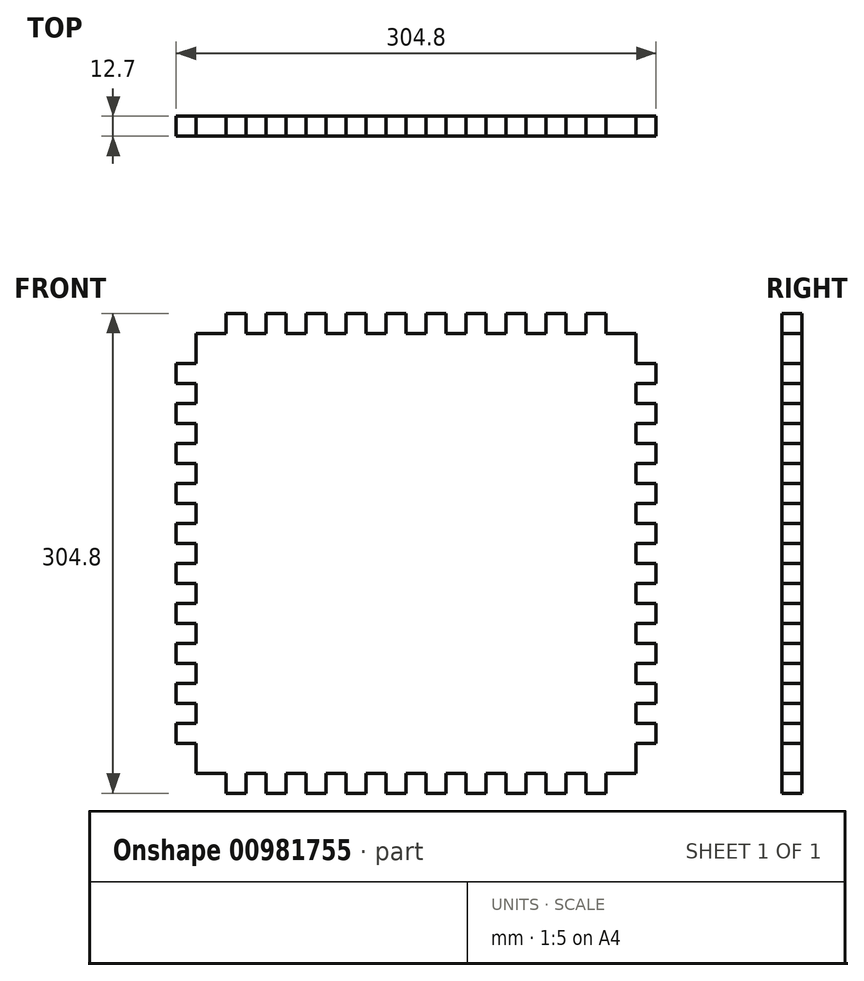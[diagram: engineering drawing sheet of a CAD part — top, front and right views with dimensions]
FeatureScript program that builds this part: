
annotation { "Feature Type Name" : "Feature", "Feature Type Description" : "" }
export const myFeature = defineFeature(function(context is Context, id is Id, definition is map)
    precondition{}
    {
        {
            var Q0;
            Q0=qCreatedBy(makeId("Front.planeOp"),FACE);
            var sketch = newSketch(context, id + "F0", { "sketchPlane" : qUnion([Q0])});
            skPoint(sketch, "E0.middle", {"position": v(0, 0) * mm});
            skLineSegment(sketch, "E1", {"start": v(-120.65, 139.7) * mm, "end": v(-120.65, 152.4) * mm});
            skLineSegment(sketch, "E2", {"start": v(-120.65, 152.4) * mm, "end": v(-107.95, 152.4) * mm});
            skLineSegment(sketch, "E3", {"start": v(-107.95, 152.4) * mm, "end": v(-107.95, 139.7) * mm});
            skLineSegment(sketch, "E4", {"start": v(-107.95, 139.7) * mm, "end": v(-95.25, 139.7) * mm});
            skLineSegment(sketch, "E5", {"start": v(-120.65, 139.7) * mm, "end": v(-139.7, 139.7) * mm});
            skLineSegment(sketch, "E6.1.0.0", {"start": v(-95.25, 152.4) * mm, "end": v(-82.55, 152.4) * mm});
            skLineSegment(sketch, "E6.1.0.1", {"start": v(-95.25, 139.7) * mm, "end": v(-95.25, 152.4) * mm});
            skLineSegment(sketch, "E6.1.0.2", {"start": v(-82.55, 139.7) * mm, "end": v(-69.85, 139.7) * mm});
            skLineSegment(sketch, "E6.1.0.3", {"start": v(-82.55, 152.4) * mm, "end": v(-82.55, 139.7) * mm});
            skLineSegment(sketch, "E6.2.0.0", {"start": v(-69.85, 152.4) * mm, "end": v(-57.15, 152.4) * mm});
            skLineSegment(sketch, "E6.2.0.1", {"start": v(-69.85, 139.7) * mm, "end": v(-69.85, 152.4) * mm});
            skLineSegment(sketch, "E6.2.0.2", {"start": v(-57.15, 139.7) * mm, "end": v(-44.45, 139.7) * mm});
            skLineSegment(sketch, "E6.2.0.3", {"start": v(-57.15, 152.4) * mm, "end": v(-57.15, 139.7) * mm});
            skLineSegment(sketch, "E6.3.0.0", {"start": v(-44.45, 152.4) * mm, "end": v(-31.75, 152.4) * mm});
            skLineSegment(sketch, "E6.3.0.1", {"start": v(-44.45, 139.7) * mm, "end": v(-44.45, 152.4) * mm});
            skLineSegment(sketch, "E6.3.0.2", {"start": v(-31.75, 139.7) * mm, "end": v(-19.05, 139.7) * mm});
            skLineSegment(sketch, "E6.3.0.3", {"start": v(-31.75, 152.4) * mm, "end": v(-31.75, 139.7) * mm});
            skLineSegment(sketch, "E6.4.0.0", {"start": v(-19.05, 152.4) * mm, "end": v(-6.35, 152.4) * mm});
            skLineSegment(sketch, "E6.4.0.1", {"start": v(-19.05, 139.7) * mm, "end": v(-19.05, 152.4) * mm});
            skLineSegment(sketch, "E6.4.0.2", {"start": v(-6.35, 139.7) * mm, "end": v(6.35, 139.7) * mm});
            skLineSegment(sketch, "E6.4.0.3", {"start": v(-6.35, 152.4) * mm, "end": v(-6.35, 139.7) * mm});
            skLineSegment(sketch, "E6.5.0.0", {"start": v(6.35, 152.4) * mm, "end": v(19.05, 152.4) * mm});
            skLineSegment(sketch, "E6.5.0.1", {"start": v(6.35, 139.7) * mm, "end": v(6.35, 152.4) * mm});
            skLineSegment(sketch, "E6.5.0.2", {"start": v(19.05, 139.7) * mm, "end": v(31.75, 139.7) * mm});
            skLineSegment(sketch, "E6.5.0.3", {"start": v(19.05, 152.4) * mm, "end": v(19.05, 139.7) * mm});
            skLineSegment(sketch, "E6.6.0.0", {"start": v(31.75, 152.4) * mm, "end": v(44.45, 152.4) * mm});
            skLineSegment(sketch, "E6.6.0.1", {"start": v(31.75, 139.7) * mm, "end": v(31.75, 152.4) * mm});
            skLineSegment(sketch, "E6.6.0.2", {"start": v(44.45, 139.7) * mm, "end": v(57.15, 139.7) * mm});
            skLineSegment(sketch, "E6.6.0.3", {"start": v(44.45, 152.4) * mm, "end": v(44.45, 139.7) * mm});
            skLineSegment(sketch, "E6.7.0.0", {"start": v(57.15, 152.4) * mm, "end": v(69.85, 152.4) * mm});
            skLineSegment(sketch, "E6.7.0.1", {"start": v(57.15, 139.7) * mm, "end": v(57.15, 152.4) * mm});
            skLineSegment(sketch, "E6.7.0.2", {"start": v(69.85, 139.7) * mm, "end": v(82.55, 139.7) * mm});
            skLineSegment(sketch, "E6.7.0.3", {"start": v(69.85, 152.4) * mm, "end": v(69.85, 139.7) * mm});
            skLineSegment(sketch, "E6.8.0.0", {"start": v(82.55, 152.4) * mm, "end": v(95.25, 152.4) * mm});
            skLineSegment(sketch, "E6.8.0.1", {"start": v(82.55, 139.7) * mm, "end": v(82.55, 152.4) * mm});
            skLineSegment(sketch, "E6.8.0.2", {"start": v(95.25, 139.7) * mm, "end": v(107.95, 139.7) * mm});
            skLineSegment(sketch, "E6.8.0.3", {"start": v(95.25, 152.4) * mm, "end": v(95.25, 139.7) * mm});
            skLineSegment(sketch, "E6.9.0.0", {"start": v(107.95, 152.4) * mm, "end": v(120.65, 152.4) * mm});
            skLineSegment(sketch, "E6.9.0.1", {"start": v(107.95, 139.7) * mm, "end": v(107.95, 152.4) * mm});
            skLineSegment(sketch, "E6.9.0.3", {"start": v(120.65, 152.4) * mm, "end": v(120.65, 139.7) * mm});
            skLineSegment(sketch, "E6.direction1", {"start": v(-120.65, 139.7) * mm, "end": v(-95.25, 139.7) * mm, "construction": true});
            skLineSegment(sketch, "E7", {"start": v(120.65, 139.7) * mm, "end": v(139.7, 139.7) * mm});
            skLineSegment(sketch, "E8.MirrorCS", {"start": v(-120.65, -139.7) * mm, "end": v(-95.25, -139.7) * mm, "construction": true});
            skLineSegment(sketch, "E9.MirrorCS", {"start": v(-95.25, -139.7) * mm, "end": v(-95.25, -152.4) * mm});
            skLineSegment(sketch, "E10.MirrorCS", {"start": v(-107.95, -152.4) * mm, "end": v(-107.95, -139.7) * mm});
            skLineSegment(sketch, "E11.MirrorCS", {"start": v(-107.95, -139.7) * mm, "end": v(-95.25, -139.7) * mm});
            skLineSegment(sketch, "E12.MirrorCS", {"start": v(-120.65, -152.4) * mm, "end": v(-107.95, -152.4) * mm});
            skLineSegment(sketch, "E13.MirrorCS", {"start": v(-95.25, -152.4) * mm, "end": v(-82.55, -152.4) * mm});
            skLineSegment(sketch, "E14.MirrorCS", {"start": v(-120.65, -139.7) * mm, "end": v(-120.65, -152.4) * mm});
            skLineSegment(sketch, "E15.MirrorCS", {"start": v(82.55, -139.7) * mm, "end": v(82.55, -152.4) * mm});
            skLineSegment(sketch, "E16.MirrorCS", {"start": v(82.55, -152.4) * mm, "end": v(95.25, -152.4) * mm});
            skLineSegment(sketch, "E17.MirrorCS", {"start": v(6.35, -152.4) * mm, "end": v(19.05, -152.4) * mm});
            skLineSegment(sketch, "E18.MirrorCS", {"start": v(-44.45, -152.4) * mm, "end": v(-31.75, -152.4) * mm});
            skLineSegment(sketch, "E19.MirrorCS", {"start": v(-31.75, -139.7) * mm, "end": v(-19.05, -139.7) * mm});
            skLineSegment(sketch, "E20.MirrorCS", {"start": v(-19.05, -152.4) * mm, "end": v(-6.35, -152.4) * mm});
            skLineSegment(sketch, "E21.MirrorCS", {"start": v(-82.55, -139.7) * mm, "end": v(-69.85, -139.7) * mm});
            skLineSegment(sketch, "E22.MirrorCS", {"start": v(-31.75, -152.4) * mm, "end": v(-31.75, -139.7) * mm});
            skLineSegment(sketch, "E23.MirrorCS", {"start": v(44.45, -152.4) * mm, "end": v(44.45, -139.7) * mm});
            skLineSegment(sketch, "E24.MirrorCS", {"start": v(31.75, -139.7) * mm, "end": v(31.75, -152.4) * mm});
            skLineSegment(sketch, "E25.MirrorCS", {"start": v(107.95, -139.7) * mm, "end": v(107.95, -152.4) * mm});
            skLineSegment(sketch, "E26.MirrorCS", {"start": v(-19.05, -139.7) * mm, "end": v(-19.05, -152.4) * mm});
            skLineSegment(sketch, "E27.MirrorCS", {"start": v(-69.85, -139.7) * mm, "end": v(-69.85, -152.4) * mm});
            skLineSegment(sketch, "E28.MirrorCS", {"start": v(107.95, -152.4) * mm, "end": v(120.65, -152.4) * mm});
            skLineSegment(sketch, "E29.MirrorCS", {"start": v(95.25, -152.4) * mm, "end": v(95.25, -139.7) * mm});
            skLineSegment(sketch, "E30.MirrorCS", {"start": v(31.75, -152.4) * mm, "end": v(44.45, -152.4) * mm});
            skLineSegment(sketch, "E31.MirrorCS", {"start": v(-6.35, -139.7) * mm, "end": v(6.35, -139.7) * mm});
            skLineSegment(sketch, "E32.MirrorCS", {"start": v(-69.85, -152.4) * mm, "end": v(-57.15, -152.4) * mm});
            skLineSegment(sketch, "E33.MirrorCS", {"start": v(69.85, -139.7) * mm, "end": v(82.55, -139.7) * mm});
            skLineSegment(sketch, "E34.MirrorCS", {"start": v(-6.35, -152.4) * mm, "end": v(-6.35, -139.7) * mm});
            skLineSegment(sketch, "E35.MirrorCS", {"start": v(57.15, -152.4) * mm, "end": v(69.85, -152.4) * mm});
            skLineSegment(sketch, "E36.MirrorCS", {"start": v(-44.45, -139.7) * mm, "end": v(-44.45, -152.4) * mm});
            skLineSegment(sketch, "E37.MirrorCS", {"start": v(-57.15, -139.7) * mm, "end": v(-44.45, -139.7) * mm});
            skLineSegment(sketch, "E38.MirrorCS", {"start": v(-120.65, -139.7) * mm, "end": v(-139.7, -139.7) * mm});
            skLineSegment(sketch, "E39.MirrorCS", {"start": v(-82.55, -152.4) * mm, "end": v(-82.55, -139.7) * mm});
            skLineSegment(sketch, "E40.MirrorCS", {"start": v(44.45, -139.7) * mm, "end": v(57.15, -139.7) * mm});
            skLineSegment(sketch, "E41.MirrorCS", {"start": v(95.25, -139.7) * mm, "end": v(107.95, -139.7) * mm});
            skLineSegment(sketch, "E42.MirrorCS", {"start": v(57.15, -139.7) * mm, "end": v(57.15, -152.4) * mm});
            skLineSegment(sketch, "E43.MirrorCS", {"start": v(69.85, -152.4) * mm, "end": v(69.85, -139.7) * mm});
            skLineSegment(sketch, "E44.MirrorCS", {"start": v(120.65, -152.4) * mm, "end": v(120.65, -139.7) * mm});
            skLineSegment(sketch, "E45.MirrorCS", {"start": v(-57.15, -152.4) * mm, "end": v(-57.15, -139.7) * mm});
            skLineSegment(sketch, "E46.MirrorCS", {"start": v(19.05, -152.4) * mm, "end": v(19.05, -139.7) * mm});
            skLineSegment(sketch, "E47.MirrorCS", {"start": v(120.65, -139.7) * mm, "end": v(139.7, -139.7) * mm});
            skLineSegment(sketch, "E48.MirrorCS", {"start": v(19.05, -139.7) * mm, "end": v(31.75, -139.7) * mm});
            skLineSegment(sketch, "E49.MirrorCS", {"start": v(6.35, -139.7) * mm, "end": v(6.35, -152.4) * mm});
            skLineSegment(sketch, "E50.MirrorCS", {"start": v(-152.4, 107.95) * mm, "end": v(-139.7, 107.95) * mm});
            skLineSegment(sketch, "E51.MirrorCS", {"start": v(-139.7, 107.95) * mm, "end": v(-139.7, 95.25) * mm});
            skLineSegment(sketch, "E52.MirrorCS", {"start": v(-152.4, 120.65) * mm, "end": v(-152.4, 107.95) * mm});
            skLineSegment(sketch, "E53.MirrorCS", {"start": v(-152.4, -107.95) * mm, "end": v(-152.4, -120.65) * mm});
            skLineSegment(sketch, "E54.MirrorCS", {"start": v(-139.7, 44.45) * mm, "end": v(-152.4, 44.45) * mm});
            skLineSegment(sketch, "E55.MirrorCS", {"start": v(-139.7, 69.85) * mm, "end": v(-152.4, 69.85) * mm});
            skLineSegment(sketch, "E56.MirrorCS", {"start": v(-152.4, -95.25) * mm, "end": v(-139.7, -95.25) * mm});
            skLineSegment(sketch, "E57.MirrorCS", {"start": v(-139.7, 6.35) * mm, "end": v(-139.7, -6.35) * mm});
            skLineSegment(sketch, "E58.MirrorCS", {"start": v(-139.7, 82.55) * mm, "end": v(-139.7, 69.85) * mm});
            skLineSegment(sketch, "E59.MirrorCS", {"start": v(-152.4, -31.75) * mm, "end": v(-152.4, -44.45) * mm});
            skLineSegment(sketch, "E60.MirrorCS", {"start": v(-139.7, -6.35) * mm, "end": v(-152.4, -6.35) * mm});
            skLineSegment(sketch, "E61.MirrorCS", {"start": v(-139.7, -95.25) * mm, "end": v(-139.7, -107.95) * mm});
            skLineSegment(sketch, "E62.MirrorCS", {"start": v(-139.7, -69.85) * mm, "end": v(-139.7, -82.55) * mm});
            skLineSegment(sketch, "E63.MirrorCS", {"start": v(-139.7, 95.25) * mm, "end": v(-152.4, 95.25) * mm});
            skLineSegment(sketch, "E64.MirrorCS", {"start": v(-139.7, 19.05) * mm, "end": v(-152.4, 19.05) * mm});
            skLineSegment(sketch, "E65.MirrorCS", {"start": v(-139.7, -31.75) * mm, "end": v(-152.4, -31.75) * mm});
            skLineSegment(sketch, "E66.MirrorCS", {"start": v(-152.4, 95.25) * mm, "end": v(-152.4, 82.55) * mm});
            skLineSegment(sketch, "E67.MirrorCS", {"start": v(-152.4, 69.85) * mm, "end": v(-152.4, 57.15) * mm});
            skLineSegment(sketch, "E68.MirrorCS", {"start": v(-152.4, 6.35) * mm, "end": v(-139.7, 6.35) * mm});
            skLineSegment(sketch, "E69.MirrorCS", {"start": v(-152.4, 31.75) * mm, "end": v(-139.7, 31.75) * mm});
            skLineSegment(sketch, "E70.MirrorCS", {"start": v(-152.4, -69.85) * mm, "end": v(-139.7, -69.85) * mm});
            skLineSegment(sketch, "E71.MirrorCS", {"start": v(-139.7, -82.55) * mm, "end": v(-152.4, -82.55) * mm});
            skLineSegment(sketch, "E72.MirrorCS", {"start": v(-152.4, 19.05) * mm, "end": v(-152.4, 6.35) * mm});
            skLineSegment(sketch, "E73.MirrorCS", {"start": v(-152.4, 82.55) * mm, "end": v(-139.7, 82.55) * mm});
            skLineSegment(sketch, "E74.MirrorCS", {"start": v(-152.4, -6.35) * mm, "end": v(-152.4, -19.05) * mm});
            skLineSegment(sketch, "E75.MirrorCS", {"start": v(-152.4, -82.55) * mm, "end": v(-152.4, -95.25) * mm});
            skLineSegment(sketch, "E76.MirrorCS", {"start": v(-152.4, -57.15) * mm, "end": v(-152.4, -69.85) * mm});
            skLineSegment(sketch, "E77.MirrorCS", {"start": v(-152.4, -120.65) * mm, "end": v(-139.7, -120.65) * mm});
            skLineSegment(sketch, "E78.MirrorCS", {"start": v(-139.7, 31.75) * mm, "end": v(-139.7, 19.05) * mm});
            skLineSegment(sketch, "E79.MirrorCS", {"start": v(-152.4, 57.15) * mm, "end": v(-139.7, 57.15) * mm});
            skLineSegment(sketch, "E80.MirrorCS", {"start": v(-139.7, -44.45) * mm, "end": v(-139.7, -57.15) * mm});
            skLineSegment(sketch, "E81.MirrorCS", {"start": v(-139.7, -19.05) * mm, "end": v(-139.7, -31.75) * mm});
            skLineSegment(sketch, "E82.MirrorCS", {"start": v(-139.7, -107.95) * mm, "end": v(-152.4, -107.95) * mm});
            skLineSegment(sketch, "E83.MirrorCS", {"start": v(-152.4, 44.45) * mm, "end": v(-152.4, 31.75) * mm});
            skLineSegment(sketch, "E84.MirrorCS", {"start": v(-152.4, -44.45) * mm, "end": v(-139.7, -44.45) * mm});
            skLineSegment(sketch, "E85.MirrorCS", {"start": v(-139.7, -120.65) * mm, "end": v(-139.7, -139.7) * mm});
            skLineSegment(sketch, "E86.MirrorCS", {"start": v(-139.7, 120.65) * mm, "end": v(-152.4, 120.65) * mm});
            skLineSegment(sketch, "E87.MirrorCS", {"start": v(-152.4, -19.05) * mm, "end": v(-139.7, -19.05) * mm});
            skLineSegment(sketch, "E88.MirrorCS", {"start": v(-139.7, -57.15) * mm, "end": v(-152.4, -57.15) * mm});
            skLineSegment(sketch, "E89.MirrorCS", {"start": v(-139.7, 120.65) * mm, "end": v(-139.7, 139.7) * mm});
            skLineSegment(sketch, "E90.MirrorCS", {"start": v(-139.7, 57.15) * mm, "end": v(-139.7, 44.45) * mm});
            skLineSegment(sketch, "E91.MirrorCS", {"start": v(139.7, -120.65) * mm, "end": v(139.7, -139.7) * mm});
            skLineSegment(sketch, "E92.MirrorCS", {"start": v(139.7, 120.65) * mm, "end": v(139.7, 139.7) * mm});
            skLineSegment(sketch, "E93.MirrorCS", {"start": v(152.4, 120.65) * mm, "end": v(152.4, 107.95) * mm});
            skLineSegment(sketch, "E94.MirrorCS", {"start": v(139.7, -31.75) * mm, "end": v(152.4, -31.75) * mm});
            skLineSegment(sketch, "E95.MirrorCS", {"start": v(139.7, -19.05) * mm, "end": v(139.7, -31.75) * mm});
            skLineSegment(sketch, "E96.MirrorCS", {"start": v(139.7, -44.45) * mm, "end": v(139.7, -57.15) * mm});
            skLineSegment(sketch, "E97.MirrorCS", {"start": v(139.7, 31.75) * mm, "end": v(139.7, 19.05) * mm});
            skLineSegment(sketch, "E98.MirrorCS", {"start": v(152.4, 107.95) * mm, "end": v(139.7, 107.95) * mm});
            skLineSegment(sketch, "E99.MirrorCS", {"start": v(152.4, -57.15) * mm, "end": v(152.4, -69.85) * mm});
            skLineSegment(sketch, "E100.MirrorCS", {"start": v(152.4, 6.35) * mm, "end": v(139.7, 6.35) * mm});
            skLineSegment(sketch, "E101.MirrorCS", {"start": v(139.7, 6.35) * mm, "end": v(139.7, -6.35) * mm});
            skLineSegment(sketch, "E102.MirrorCS", {"start": v(152.4, 95.25) * mm, "end": v(152.4, 82.55) * mm});
            skLineSegment(sketch, "E103.MirrorCS", {"start": v(152.4, -107.95) * mm, "end": v(152.4, -120.65) * mm});
            skLineSegment(sketch, "E104.MirrorCS", {"start": v(152.4, -95.25) * mm, "end": v(139.7, -95.25) * mm});
            skLineSegment(sketch, "E105.MirrorCS", {"start": v(139.7, 120.65) * mm, "end": v(152.4, 120.65) * mm});
            skLineSegment(sketch, "E106.MirrorCS", {"start": v(152.4, -69.85) * mm, "end": v(139.7, -69.85) * mm});
            skLineSegment(sketch, "E107.MirrorCS", {"start": v(139.7, 57.15) * mm, "end": v(139.7, 44.45) * mm});
            skLineSegment(sketch, "E108.MirrorCS", {"start": v(139.7, -107.95) * mm, "end": v(152.4, -107.95) * mm});
            skLineSegment(sketch, "E109.MirrorCS", {"start": v(152.4, -120.65) * mm, "end": v(139.7, -120.65) * mm});
            skLineSegment(sketch, "E110.MirrorCS", {"start": v(152.4, -6.35) * mm, "end": v(152.4, -19.05) * mm});
            skLineSegment(sketch, "E111.MirrorCS", {"start": v(152.4, 69.85) * mm, "end": v(152.4, 57.15) * mm});
            skLineSegment(sketch, "E112.MirrorCS", {"start": v(152.4, -31.75) * mm, "end": v(152.4, -44.45) * mm});
            skLineSegment(sketch, "E113.MirrorCS", {"start": v(139.7, -82.55) * mm, "end": v(152.4, -82.55) * mm});
            skLineSegment(sketch, "E114.MirrorCS", {"start": v(152.4, -82.55) * mm, "end": v(152.4, -95.25) * mm});
            skLineSegment(sketch, "E115.MirrorCS", {"start": v(139.7, -57.15) * mm, "end": v(152.4, -57.15) * mm});
            skLineSegment(sketch, "E116.MirrorCS", {"start": v(139.7, 69.85) * mm, "end": v(152.4, 69.85) * mm});
            skLineSegment(sketch, "E117.MirrorCS", {"start": v(139.7, 19.05) * mm, "end": v(152.4, 19.05) * mm});
            skLineSegment(sketch, "E118.MirrorCS", {"start": v(152.4, 82.55) * mm, "end": v(139.7, 82.55) * mm});
            skLineSegment(sketch, "E119.MirrorCS", {"start": v(139.7, -95.25) * mm, "end": v(139.7, -107.95) * mm});
            skLineSegment(sketch, "E120.MirrorCS", {"start": v(152.4, 31.75) * mm, "end": v(139.7, 31.75) * mm});
            skLineSegment(sketch, "E121.MirrorCS", {"start": v(139.7, 95.25) * mm, "end": v(152.4, 95.25) * mm});
            skLineSegment(sketch, "E122.MirrorCS", {"start": v(139.7, 82.55) * mm, "end": v(139.7, 69.85) * mm});
            skLineSegment(sketch, "E123.MirrorCS", {"start": v(139.7, 44.45) * mm, "end": v(152.4, 44.45) * mm});
            skLineSegment(sketch, "E124.MirrorCS", {"start": v(152.4, -44.45) * mm, "end": v(139.7, -44.45) * mm});
            skLineSegment(sketch, "E125.MirrorCS", {"start": v(139.7, -69.85) * mm, "end": v(139.7, -82.55) * mm});
            skLineSegment(sketch, "E126.MirrorCS", {"start": v(152.4, -19.05) * mm, "end": v(139.7, -19.05) * mm});
            skLineSegment(sketch, "E127.MirrorCS", {"start": v(139.7, -6.35) * mm, "end": v(152.4, -6.35) * mm});
            skLineSegment(sketch, "E128.MirrorCS", {"start": v(152.4, 57.15) * mm, "end": v(139.7, 57.15) * mm});
            skLineSegment(sketch, "E129.MirrorCS", {"start": v(152.4, 19.05) * mm, "end": v(152.4, 6.35) * mm});
            skLineSegment(sketch, "E130.MirrorCS", {"start": v(152.4, 44.45) * mm, "end": v(152.4, 31.75) * mm});
            skLineSegment(sketch, "E131.MirrorCS", {"start": v(139.7, 107.95) * mm, "end": v(139.7, 95.25) * mm});
            skSolve(sketch);
        }
        {
            var Q0;
            Q0=makeQuery(id+"F0.imprint","IMPRINT",FACE,{"disambiguationData":[TD([[makeQuery(id+"F0.imprint","IMPRINT",EDGE,{"derivedFrom":sQuery(id+"F0.wireOp",EDGE,"E1")}),-1.0]])]});
            extrude(context, id + "F1", {"entities" : qUnion([Q0]), "depth" : 12.7 * mm, "offsetDistance" : 25.4 * mm});
        }
    });
